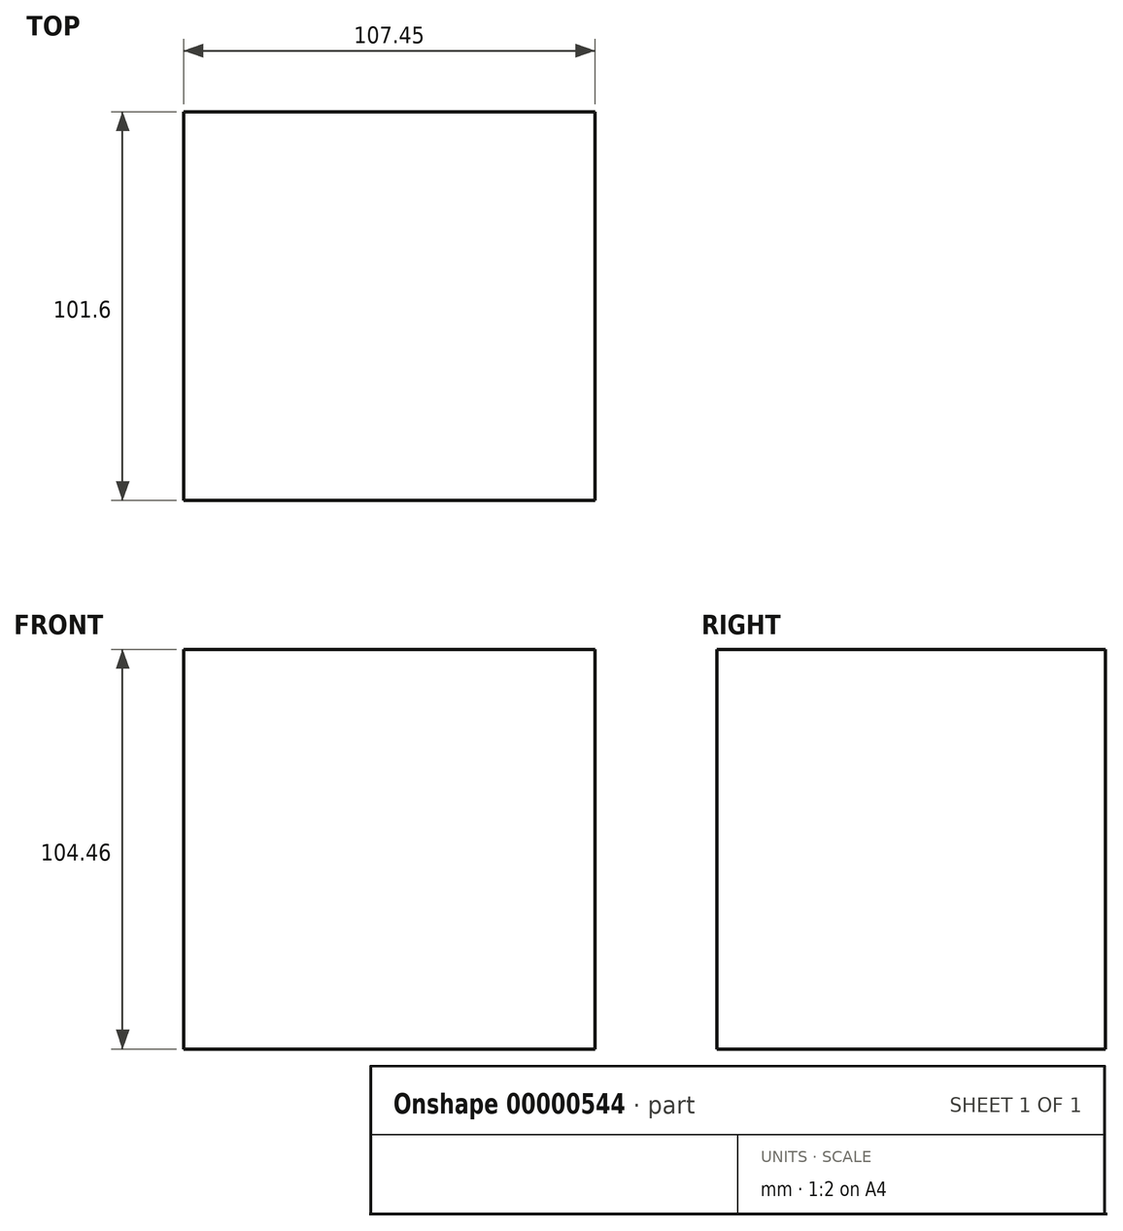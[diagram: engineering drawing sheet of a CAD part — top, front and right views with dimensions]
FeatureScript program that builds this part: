
annotation { "Feature Type Name" : "Feature", "Feature Type Description" : "" }
export const myFeature = defineFeature(function(context is Context, id is Id, definition is map)
    precondition{}
    {
        {
            var Q0;
            Q0=qCreatedBy(makeId("Front.planeOp"),FACE);
            var sketch = newSketch(context, id + "F0", { "sketchPlane" : qUnion([Q0])});
            skLineSegment(sketch, "E0.bottom", {"start": v(-52.35, 46.25) * mm, "end": v(55.1, 46.25) * mm});
            skLineSegment(sketch, "E0.top", {"start": v(-52.35, -58.21) * mm, "end": v(55.1, -58.21) * mm});
            skLineSegment(sketch, "E0.left", {"start": v(-52.35, 46.25) * mm, "end": v(-52.35, -58.21) * mm});
            skLineSegment(sketch, "E0.right", {"start": v(55.1, 46.25) * mm, "end": v(55.1, -58.21) * mm});
            skSolve(sketch);
        }
        {
            var Q0;
            Q0=makeQuery(id+"F0.imprint","IMPRINT",FACE,{"disambiguationData":[TD([[makeQuery(id+"F0.imprint","IMPRINT",EDGE,{"derivedFrom":sQuery(id+"F0.wireOp",EDGE,"E0.bottom")}),-1.0]])]});
            extrude(context, id + "F1", {"entities" : qUnion([Q0]), "depth" : 101.6 * mm});
        }
        {
            var Q0;
            Q0=makeQuery(id+"F0.imprint","IMPRINT",FACE,{"disambiguationData":[TD([[makeQuery(id+"F0.imprint","IMPRINT",EDGE,{"derivedFrom":sQuery(id+"F0.wireOp",EDGE,"E0.bottom")}),-1.0]])]});
            extrude(context, id + "F2", {"entities" : qUnion([Q0]), "operationType" : NewBodyOperationType.ADD, "depth" : 25.4 * mm});
        }
    });
